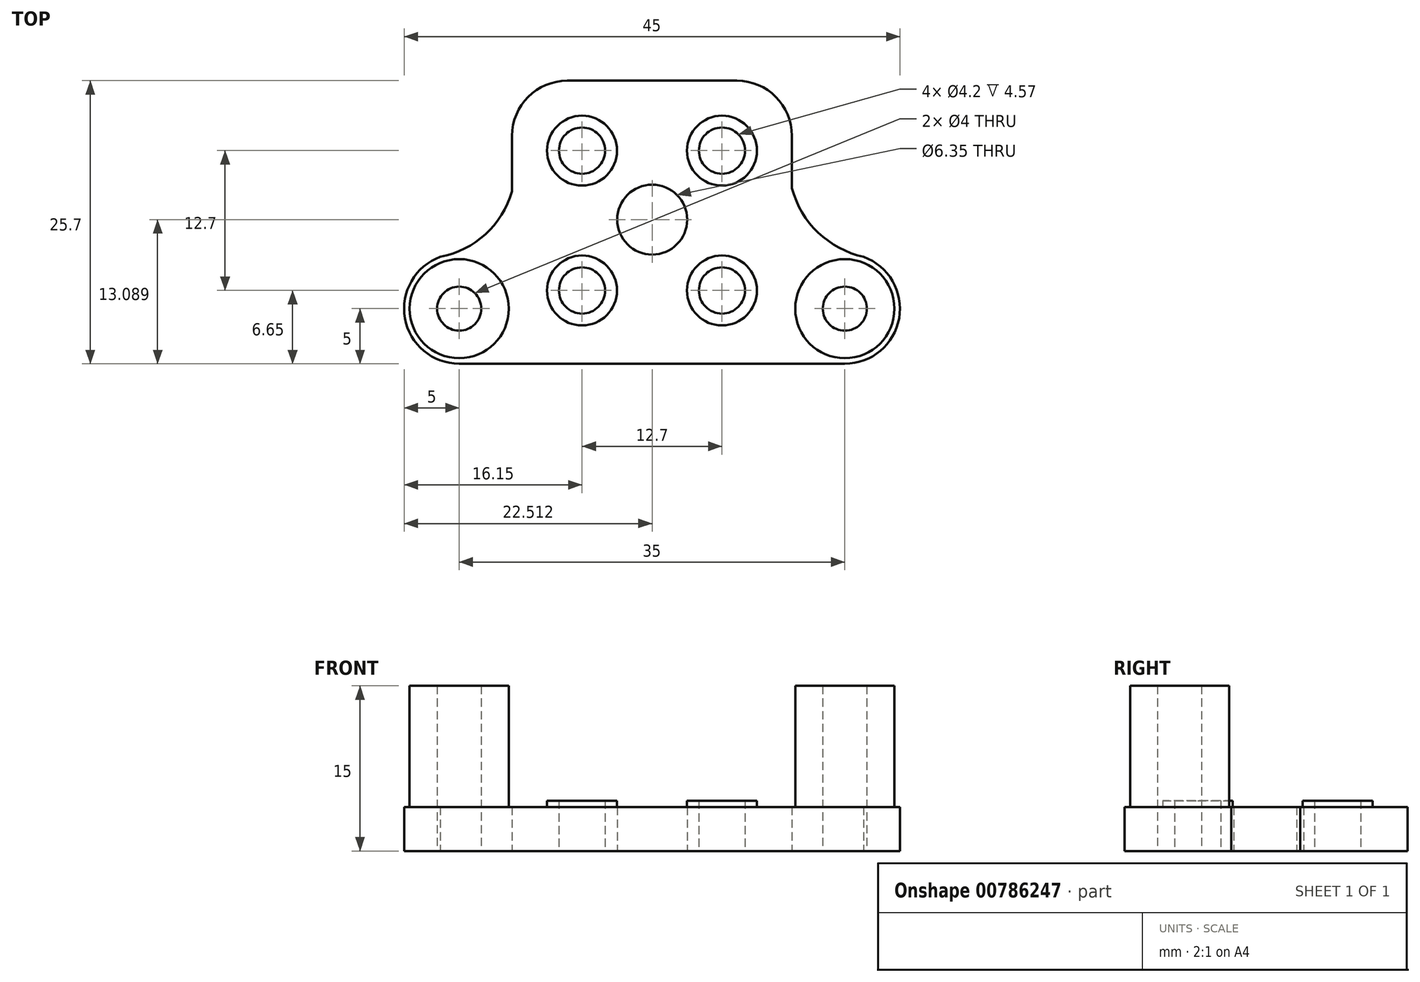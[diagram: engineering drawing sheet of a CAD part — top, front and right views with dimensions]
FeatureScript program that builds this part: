
annotation { "Feature Type Name" : "Feature", "Feature Type Description" : "" }
export const myFeature = defineFeature(function(context is Context, id is Id, definition is map)
    precondition{}
    {
        {
            var Q0;
            Q0=qCreatedBy(makeId("Top.planeOp"),FACE);
            var sketch = newSketch(context, id + "F0", { "sketchPlane" : qUnion([Q0])});
            skCircle(sketch, "E0", {"center": v(0, 0) * mm, "radius": 3.25 * mm});
            skCircle(sketch, "E1", {"center": v(0, 0) * mm, "radius": 3.5 * mm});
            skSolve(sketch);
        }
        {
            var Q0;
            Q0=makeQuery(id+"F0.imprint","IMPRINT",FACE,{"disambiguationData":[TD([[makeQuery(id+"F0.imprint","IMPRINT",EDGE,{"derivedFrom":sQuery(id+"F0.wireOp",EDGE,"E0")}),-1.0]])]});
            var sketch = newSketch(context, id + "F1", { "sketchPlane" : qUnion([Q0])});
            skLineSegment(sketch, "E2.bottom", {"start": v(-7.7, 12.7) * mm, "end": v(7.7, 12.7) * mm});
            skLineSegment(sketch, "E2.top", {"start": v(7.7, -12.7) * mm, "end": v(12.7, -12.7) * mm});
            skLineSegment(sketch, "E2.left", {"start": v(-12.7, 7.7) * mm, "end": v(-12.7, 0.06) * mm});
            skLineSegment(sketch, "E2.right", {"start": v(12.7, 7.7) * mm, "end": v(12.7, -6.6) * mm});
            skArc(sketch, "E3", {"start": v(-7.7, 12.7) * mm, "mid": v(-11.23, 11.24) * mm, "end": v(-12.7, 7.7) * mm});
            skArc(sketch, "E4", {"start": v(12.7, 7.7) * mm, "mid": v(11.25, 11.24) * mm, "end": v(7.7, 12.7) * mm});
            skCircle(sketch, "E5", {"center": v(-17.5, -8) * mm, "radius": 2 * mm});
            skArc(sketch, "E6", {"start": v(-19.2, -3.3) * mm, "mid": v(-20.91, -11.65) * mm, "end": v(-12.7, -9.4) * mm});
            skCircle(sketch, "E7", {"center": v(17.5, -8) * mm, "radius": 2 * mm});
            skPoint(sketch, "E8.orphan", {"position": v(-22.68, -3.3) * mm});
            skLineSegment(sketch, "E9", {"start": v(-17.5, -13) * mm, "end": v(17.5, -13) * mm});
            skPoint(sketch, "E10.center.orphan", {"position": v(-7.7, -7.7) * mm});
            skArc(sketch, "E11.trimOffspring", {"start": v(12.7, -9.4) * mm, "mid": v(20.93, -11.65) * mm, "end": v(19.22, -3.3) * mm});
            skPoint(sketch, "E12.center.orphan", {"position": v(7.7, -7.7) * mm});
            skLineSegment(sketch, "E13.trimOffspring", {"start": v(-12.7, -9.4) * mm, "end": v(-12.7, -12.7) * mm});
            skLineSegment(sketch, "E14.trimOffspring", {"start": v(12.7, -9.4) * mm, "end": v(12.7, -12.7) * mm});
            skCircle(sketch, "E15", {"center": v(-6.34, 6.35) * mm, "radius": 2.1 * mm});
            skCircle(sketch, "E16", {"center": v(-6.34, 6.35) * mm, "radius": 3.17 * mm});
            skCircle(sketch, "E17", {"center": v(6.36, 6.35) * mm, "radius": 2.1 * mm});
            skCircle(sketch, "E18", {"center": v(6.36, 6.35) * mm, "radius": 3.17 * mm});
            skCircle(sketch, "E19", {"center": v(-6.34, -6.35) * mm, "radius": 2.1 * mm});
            skCircle(sketch, "E20", {"center": v(6.36, -6.35) * mm, "radius": 2.1 * mm});
            skCircle(sketch, "E21", {"center": v(-6.34, -6.35) * mm, "radius": 3.17 * mm});
            skCircle(sketch, "E22", {"center": v(6.36, -6.35) * mm, "radius": 3.17 * mm});
            skLineSegment(sketch, "E23.trimOffspring", {"start": v(-6.34, -9.53) * mm, "end": v(-6.34, -10.75) * mm});
            skCircle(sketch, "E24", {"center": v(0.02, 0.09) * mm, "radius": 3.17 * mm});
            skCircle(sketch, "E25", {"center": v(17.5, -8) * mm, "radius": 4.5 * mm});
            skCircle(sketch, "E26", {"center": v(-17.5, -8) * mm, "radius": 4.5 * mm});
            skArc(sketch, "E27", {"start": v(12.7, 2.94) * mm, "mid": v(15.09, -1.1) * mm, "end": v(19.22, -3.3) * mm});
            skArc(sketch, "E28", {"start": v(-19.2, -3.3) * mm, "mid": v(-15.11, -1.24) * mm, "end": v(-12.7, 2.63) * mm});
            skSolve(sketch);
        }
        {
            var Q0;
            Q0 = qSketchRegion(id + "F1", true);
            extrude(context, id + "F2", {"entities" : qUnion([Q0]), "depth" : 4 * mm, "offsetDistance" : 25 * mm});
        }
        {
            var Q0;
            Q0=makeQuery(id+"F1.imprint","IMPRINT",FACE,{"disambiguationData":[TD([[makeQuery(id+"F1.imprint","IMPRINT",EDGE,{"derivedFrom":sQuery(id+"F1.wireOp",EDGE,"E15")}),-1.0]])]});
            extrude(context, id + "F3", {"entities" : qUnion([Q0]), "operationType" : NewBodyOperationType.ADD, "depth" : 4.57 * mm, "offsetDistance" : 25 * mm});
        }
        {
            var Q0;
            Q0=makeQuery(id+"F1.imprint","IMPRINT",FACE,{"disambiguationData":[TD([[makeQuery(id+"F1.imprint","IMPRINT",EDGE,{"derivedFrom":sQuery(id+"F1.wireOp",EDGE,"E17")}),-1.0]])]});
            extrude(context, id + "F4", {"entities" : qUnion([Q0]), "operationType" : NewBodyOperationType.ADD, "depth" : 4.57 * mm, "offsetDistance" : 25 * mm});
        }
        {
            var Q0;
            Q0=makeQuery(id+"F1.imprint","IMPRINT",FACE,{"disambiguationData":[TD([[makeQuery(id+"F1.imprint","IMPRINT",EDGE,{"derivedFrom":sQuery(id+"F1.wireOp",EDGE,"E20")}),-1.0]])]});
            extrude(context, id + "F5", {"entities" : qUnion([Q0]), "operationType" : NewBodyOperationType.ADD, "depth" : 4.57 * mm, "offsetDistance" : 25 * mm});
        }
        {
            var Q0;
            Q0=makeQuery(id+"F1.imprint","IMPRINT",FACE,{"disambiguationData":[TD([[makeQuery(id+"F1.imprint","IMPRINT",EDGE,{"derivedFrom":sQuery(id+"F1.wireOp",EDGE,"E19")}),-1.0]])]});
            extrude(context, id + "F6", {"entities" : qUnion([Q0]), "operationType" : NewBodyOperationType.ADD, "depth" : 4.57 * mm, "offsetDistance" : 25 * mm});
        }
        {
            var Q0;
            Q0=makeQuery(id+"F1.imprint","IMPRINT",FACE,{"disambiguationData":[TD([[makeQuery(id+"F1.imprint","IMPRINT",EDGE,{"derivedFrom":sQuery(id+"F1.wireOp",EDGE,"E5")}),-1.0]])]});
            extrude(context, id + "F7", {"entities" : qUnion([Q0]), "operationType" : NewBodyOperationType.ADD, "depth" : 15 * mm, "offsetDistance" : 25 * mm});
        }
        {
            var Q0;
            Q0=makeQuery(id+"F1.imprint","IMPRINT",FACE,{"disambiguationData":[TD([[makeQuery(id+"F1.imprint","IMPRINT",EDGE,{"derivedFrom":sQuery(id+"F1.wireOp",EDGE,"E7")}),-1.0]])]});
            extrude(context, id + "F8", {"entities" : qUnion([Q0]), "operationType" : NewBodyOperationType.ADD, "depth" : 15 * mm, "offsetDistance" : 25 * mm});
        }
    });
